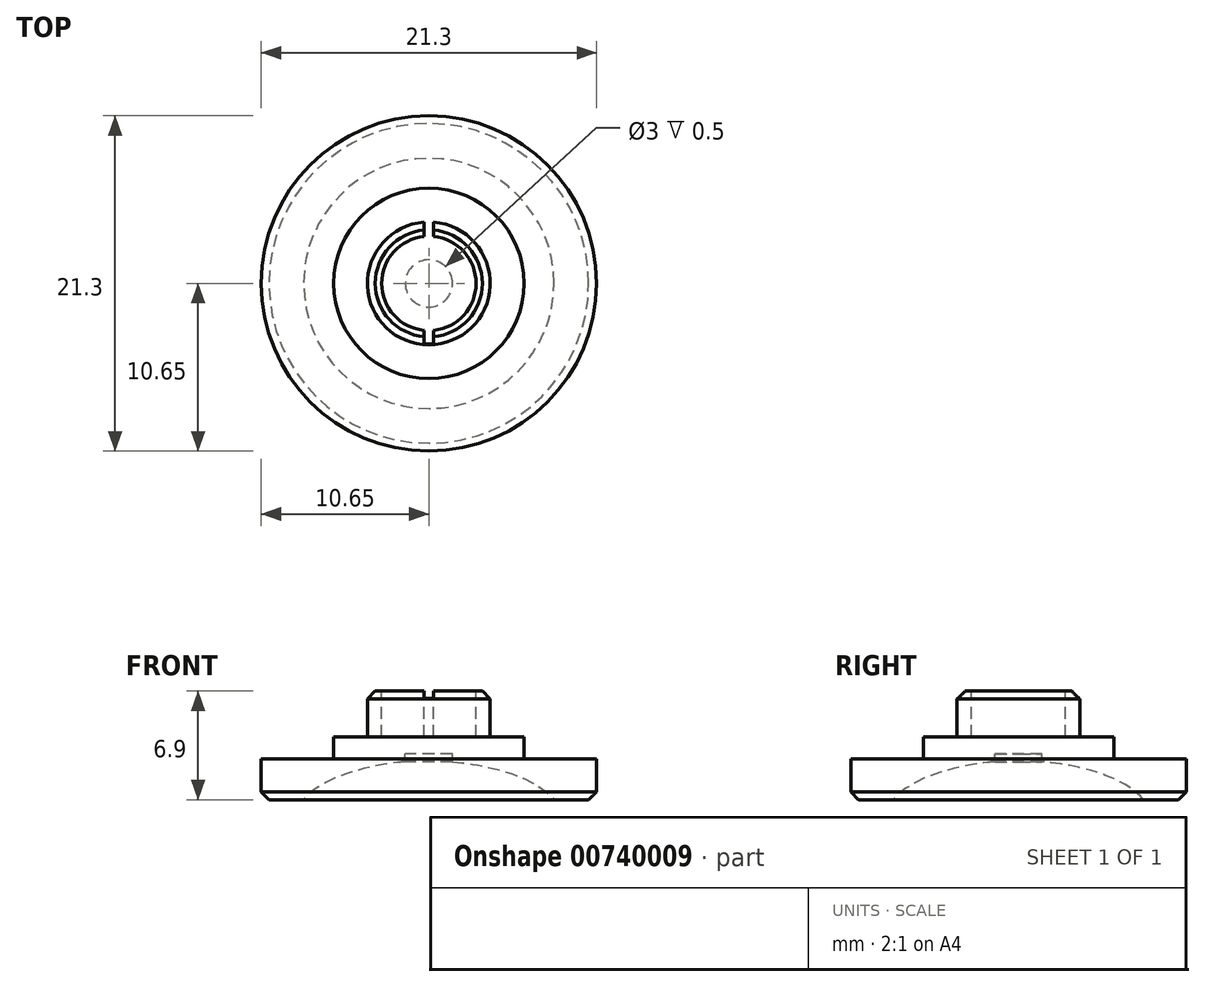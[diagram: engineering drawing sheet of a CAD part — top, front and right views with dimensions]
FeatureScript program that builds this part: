
annotation { "Feature Type Name" : "Feature", "Feature Type Description" : "" }
export const myFeature = defineFeature(function(context is Context, id is Id, definition is map)
    precondition{}
    {
        {
            var Q0;
            Q0=qCreatedBy(makeId("Front.planeOp"),FACE);
            var sketch = newSketch(context, id + "F0", { "sketchPlane" : qUnion([Q0])});
            skLineSegment(sketch, "E0", {"start": v(0, 0) * mm, "end": v(7.95, 0) * mm});
            skLineSegment(sketch, "E1", {"start": v(7.95, 0) * mm, "end": v(10.65, 0) * mm});
            skLineSegment(sketch, "E2", {"start": v(10.65, 0) * mm, "end": v(10.65, 2.6) * mm});
            skLineSegment(sketch, "E3", {"start": v(10.65, 2.6) * mm, "end": v(6.05, 2.6) * mm});
            skLineSegment(sketch, "E4", {"start": v(6.05, 2.6) * mm, "end": v(6.05, 4) * mm});
            skLineSegment(sketch, "E5", {"start": v(6.05, 4) * mm, "end": v(3.9, 4) * mm});
            skLineSegment(sketch, "E6", {"start": v(3.9, 4) * mm, "end": v(3.9, 6.9) * mm});
            skLineSegment(sketch, "E7", {"start": v(3.9, 6.9) * mm, "end": v(0, 6.9) * mm});
            skLineSegment(sketch, "E8", {"start": v(0, 6.9) * mm, "end": v(0, 0) * mm});
            skLineSegment(sketch, "E9", {"start": v(0, 0) * mm, "end": v(0, 2.5) * mm});
            skFitSpline(sketch, "E10", {"points": [v(0, 2.5) * mm, v(7.95, 0) * mm], "startDerivative": vector(7.15, -0.05) * mm, "endDerivative": vector(4.36, -5.49) * mm});
            skLineSegment(sketch, "E11", {"start": v(0, 2.92) * mm, "end": v(1.5, 2.92) * mm});
            skLineSegment(sketch, "E12", {"start": v(1.5, 2.92) * mm, "end": v(1.5, 2.42) * mm});
            skSolve(sketch);
        }
        {
            var Q0;
            {var subQ4=sQuery(id+"F0.wireOp",EDGE,"E1");Q0=makeQuery(id+"F0.imprint","IMPRINT",FACE,{"disambiguationData":[TD([[makeQuery(id+"F0.imprint","IMPRINT",EDGE,{"derivedFrom":subQ4}),1.0]])]});}
            var Q1;
            Q1=sQuery(id+"F0.wireOp",EDGE,"E8");
            revolve(context, id + "F1", {"surfaceOperationType" : NewSurfaceOperationType.NEW, "entities" : qUnion([Q0]), "axis" : qUnion([Q1]), "revolveType" : RevolveType.FULL});
        }
        {
            var Q0;
            Q0=makeQuery(id+"F1.opRevolve","SWEPT_EDGE",EDGE,{"disambiguationData":[OSD([sQuery(id+"F0.wireOp",EDGE,"E6"),sQuery(id+"F0.wireOp",EDGE,"E7")])]});
            chamfer(context, id + "F2", {"entities" : qUnion([Q0]), "width" : .5 * mm, "tangentPropagation" : true});
        }
        {
            var Q0;
            Q0=makeQuery(id+"F1.opRevolve","SWEPT_EDGE",EDGE,{"disambiguationData":[OSD([sQuery(id+"F0.wireOp",EDGE,"E1"),sQuery(id+"F0.wireOp",EDGE,"E2")])]});
            chamfer(context, id + "F3", {"entities" : qUnion([Q0]), "width" : .5 * mm, "tangentPropagation" : true});
        }
        {
            var Q0;
            Q0=qCreatedBy(makeId("Top.planeOp"),FACE);
            cPlane(context, id + "F4", {"entities" : qUnion([Q0]), "cplaneType" : CPlaneType.OFFSET, "offset" : 6.9 * mm, "width" : 150 * mm, "height" : 150 * mm});
        }
        {
            var Q0;
            Q0=qCreatedBy(id+"F4.planeOp",FACE);
            var sketch = newSketch(context, id + "F5", { "sketchPlane" : qUnion([Q0])});
            skCircle(sketch, "E13", {"center": v(0, 0) * mm, "radius": 3 * mm});
            skLineSegment(sketch, "E14", {"start": v(0, 0) * mm, "end": v(0.3, 0) * mm});
            skLineSegment(sketch, "E15", {"start": v(0, 0) * mm, "end": v(-0.3, 0) * mm});
            skLineSegment(sketch, "E16", {"start": v(0.3, 0) * mm, "end": v(0.3, -3.85) * mm});
            skLineSegment(sketch, "E17", {"start": v(0.3, 0) * mm, "end": v(0.3, 4.03) * mm});
            skLineSegment(sketch, "E18.bottom", {"start": v(-0.3, 0) * mm, "end": v(0.3, 0) * mm});
            skLineSegment(sketch, "E18.top", {"start": v(-0.3, 4.03) * mm, "end": v(0.3, 4.03) * mm});
            skLineSegment(sketch, "E18.left", {"start": v(-0.3, 0) * mm, "end": v(-0.3, 4.03) * mm});
            skLineSegment(sketch, "E19.top", {"start": v(-0.3, -3.85) * mm, "end": v(0.3, -3.85) * mm});
            skLineSegment(sketch, "E19.left", {"start": v(-0.3, 0) * mm, "end": v(-0.3, -3.85) * mm});
            skSolve(sketch);
        }
        {
            var Q0;
            Q0 = qSketchRegion(id + "F5", true);
            extrude(context, id + "F6", {"entities" : qUnion([Q0]), "operationType" : NewBodyOperationType.REMOVE, "oppositeDirection" : true, "depth" : 2.9 * mm, "offsetDistance" : 25 * mm});
        }
    });
